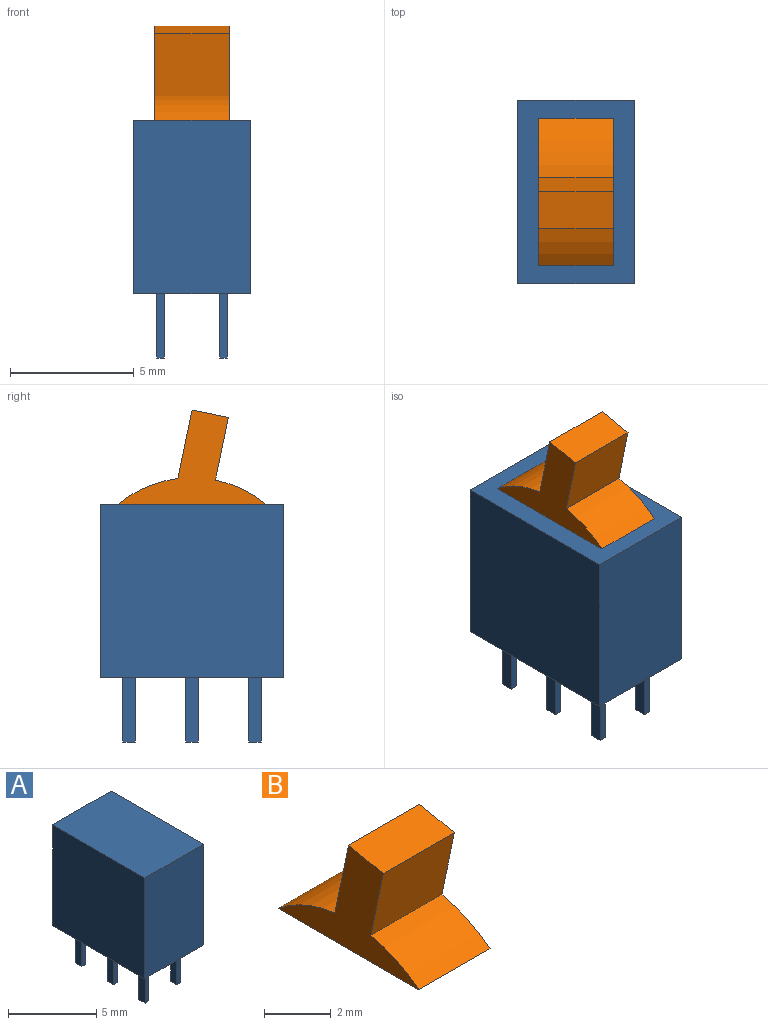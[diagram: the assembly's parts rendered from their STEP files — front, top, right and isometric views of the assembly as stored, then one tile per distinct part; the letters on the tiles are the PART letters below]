
ASSEMBLY  parts=2 mates=1
PART A: 36 faces, bbox 4.7x7.4x9.6 mm
  f0: plane 7.4x4.7mm, normal (0,0,-1), area 33.9mm2, adj f1,f3,f4,f5,f7,f8,f9,f10
  f1: plane 7x4.7mm, normal (0,1,0), area 32.9mm2, adj f0,f2,f4,f20
  f2: plane 7.4x4.7mm, normal (0,0,1), area 34.8mm2, adj f1,f3,f4,f20
  f3: plane 7x4.7mm, normal (0,-1,0), area 32.9mm2, adj f0,f2,f4,f20
  f4: plane 7.4x7mm, normal (1,0,0), area 51.8mm2, adj f0,f1,f2,f3
  f5: plane 2.6x0.3mm, normal (0,-1,0), area 0.8mm2, adj f0,f6,f8,f9
  f6: plane 0.5x0.3mm, normal (0,0,-1), area 0.2mm2, adj f5,f7,f8,f9
  f7: plane 2.6x0.3mm, normal (0,1,0), area 0.8mm2, adj f0,f6,f8,f9
  f8: plane 2.6x0.5mm, normal (1,0,0), area 1.3mm2, adj f0,f5,f6,f7
  f9: plane 2.6x0.5mm, normal (-1,0,0), area 1.3mm2, adj f0,f5,f6,f7
  f10: plane 2.6x0.3mm, normal (0,-1,0), area 0.8mm2, adj f0,f11,f13,f14
  f11: plane 0.5x0.3mm, normal (0,0,-1), area 0.2mm2, adj f10,f12,f13,f14
  f12: plane 2.6x0.3mm, normal (0,1,0), area 0.8mm2, adj f0,f11,f13,f14
  f13: plane 2.6x0.5mm, normal (1,0,0), area 1.3mm2, adj f0,f10,f11,f12
  f14: plane 2.6x0.5mm, normal (-1,0,0), area 1.3mm2, adj f0,f10,f11,f12
  f15: plane 0.5x0.3mm, normal (0,0,-1), area 0.2mm2, adj f16,f17,f18,f19
  f16: plane 2.6x0.3mm, normal (0,1,0), area 0.8mm2, adj f0,f15,f18,f19
  f17: plane 2.6x0.3mm, normal (0,-1,0), area 0.8mm2, adj f0,f15,f18,f19
  f18: plane 2.6x0.5mm, normal (1,0,0), area 1.3mm2, adj f0,f15,f16,f17
  f19: plane 2.6x0.5mm, normal (-1,0,0), area 1.3mm2, adj f0,f15,f16,f17
  f20: plane 7.4x7mm, normal (-1,0,0), area 51.8mm2, adj f0,f1,f2,f3
  f21: plane 2.6x0.3mm, normal (0,-1,0), area 0.8mm2, adj f0,f22,f24,f25
  f22: plane 0.5x0.3mm, normal (0,0,-1), area 0.2mm2, adj f21,f23,f24,f25
  f23: plane 2.6x0.3mm, normal (0,1,0), area 0.8mm2, adj f0,f22,f24,f25
  f24: plane 2.6x0.5mm, normal (-1,0,0), area 1.3mm2, adj f0,f21,f22,f23
  f25: plane 2.6x0.5mm, normal (1,0,0), area 1.3mm2, adj f0,f21,f22,f23
  f26: plane 2.6x0.3mm, normal (0,-1,0), area 0.8mm2, adj f0,f27,f29,f30
  f27: plane 0.5x0.3mm, normal (0,0,-1), area 0.2mm2, adj f26,f28,f29,f30
  f28: plane 2.6x0.3mm, normal (0,1,0), area 0.8mm2, adj f0,f27,f29,f30
  f29: plane 2.6x0.5mm, normal (-1,0,0), area 1.3mm2, adj f0,f26,f27,f28
  f30: plane 2.6x0.5mm, normal (1,0,0), area 1.3mm2, adj f0,f26,f27,f28
  f31: plane 0.5x0.3mm, normal (0,0,-1), area 0.2mm2, adj f32,f33,f34,f35
  f32: plane 2.6x0.3mm, normal (0,1,0), area 0.8mm2, adj f0,f31,f34,f35
  f33: plane 2.6x0.3mm, normal (0,-1,0), area 0.8mm2, adj f0,f31,f34,f35
  f34: plane 2.6x0.5mm, normal (-1,0,0), area 1.3mm2, adj f0,f31,f32,f33
  f35: plane 2.6x0.5mm, normal (1,0,0), area 1.3mm2, adj f0,f31,f32,f33
PART B: 8 faces, bbox 3x6x3.8 mm
  f0: plane 3x2.52mm, normal (0,-0.98,-0.2), area 7.7mm2, adj f1,f5,f6,f7
  f1: cylinder r=4.67mm len=3mm, axis (-1,0,0), area 6.8mm2, adj f0,f2,f6,f7
  f2: plane 5.95x3mm, normal (0,0,-1), area 17.9mm2, adj f1,f3,f6,f7
  f3: cylinder r=4.67mm len=3mm, axis (-1,0,0), area 8mm2, adj f2,f4,f6,f7
  f4: plane 3x2.76mm, normal (0,0.98,0.2), area 8.5mm2, adj f3,f5,f6,f7
  f5: plane 3x1.47mm, normal (0,-0.2,0.98), area 4.5mm2, adj f0,f4,f6,f7
  f6: plane 5.95x3.8mm, normal (1,0,0), area 8.3mm2, adj f0,f1,f2,f3,f4,f5
  f7: plane 5.95x3.8mm, normal (-1,0,0), area 8.3mm2, adj f0,f1,f2,f3,f4,f5
PLACE A at identity fixed
PLACE B at identity
MATE fastened B.f2 <-> A.f2  axis (0,0,-1) through (0,0,3.5)mm
